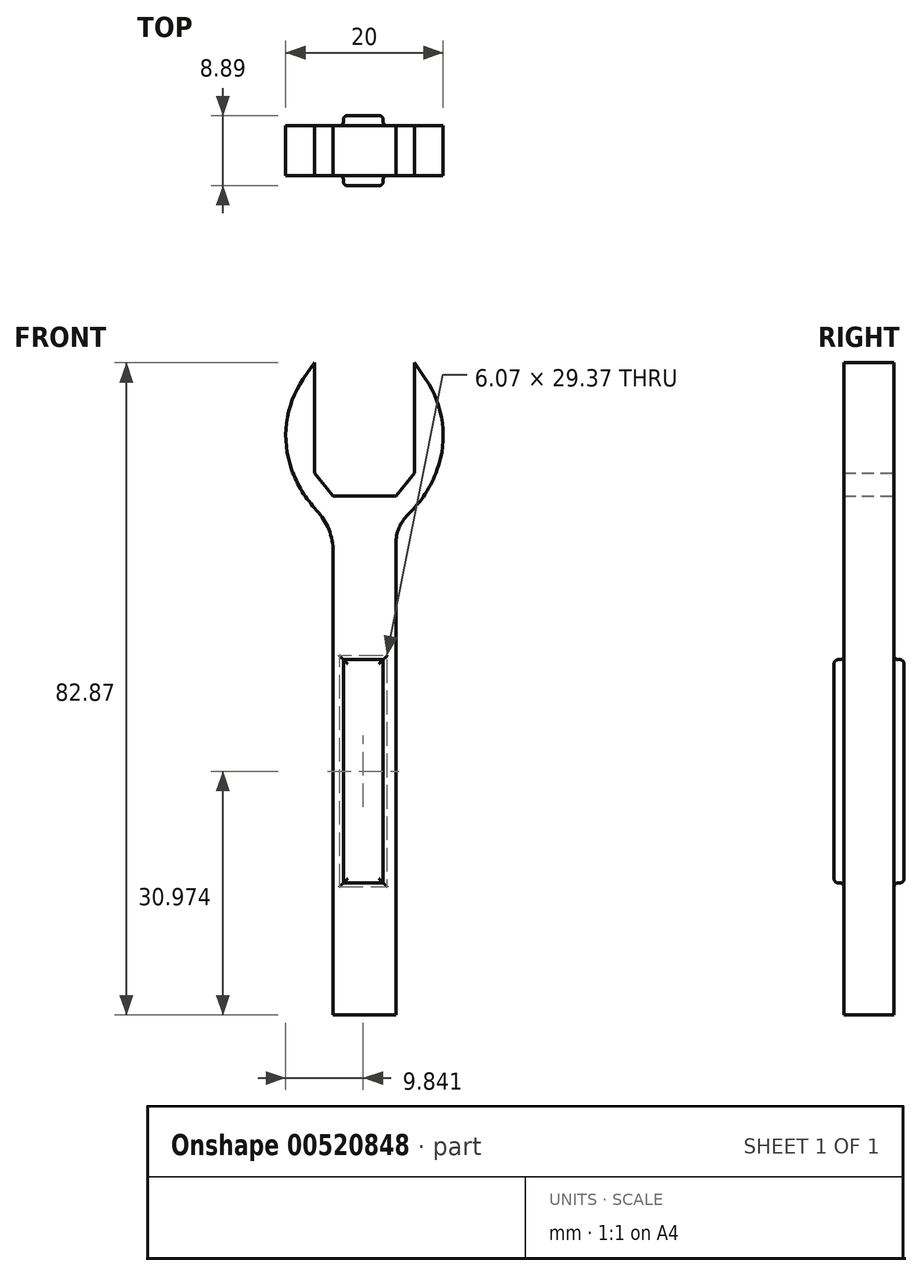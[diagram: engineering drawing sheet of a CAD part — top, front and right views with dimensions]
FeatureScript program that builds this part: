
annotation { "Feature Type Name" : "Feature", "Feature Type Description" : "" }
export const myFeature = defineFeature(function(context is Context, id is Id, definition is map)
    precondition{}
    {
        {
            var Q0;
            Q0=qCreatedBy(makeId("Front.planeOp"),FACE);
            var sketch = newSketch(context, id + "F0", { "sketchPlane" : qUnion([Q0])});
            skLineSegment(sketch, "E0", {"start": v(-17.48, 44.08) * mm, "end": v(-17.48, -18.2) * mm});
            skLineSegment(sketch, "E1", {"start": v(-9.5, -18.2) * mm, "end": v(-9.5, 44.08) * mm});
            skLineSegment(sketch, "E2", {"start": v(-17.48, 44.08) * mm, "end": v(-9.5, 44.08) * mm});
            skLineSegment(sketch, "E3", {"start": v(-9.5, 47.76) * mm, "end": v(-17.48, 47.76) * mm});
            skLineSegment(sketch, "E4", {"start": v(-17.48, 47.76) * mm, "end": v(-19.84, 50.66) * mm});
            skLineSegment(sketch, "E5", {"start": v(-19.84, 50.66) * mm, "end": v(-19.84, 59.78) * mm});
            skLineSegment(sketch, "E6", {"start": v(-19.84, 59.78) * mm, "end": v(-23.2, 59.78) * mm});
            skArc(sketch, "E7", {"start": v(-23.2, 59.78) * mm, "mid": v(-22.72, 51.06) * mm, "end": v(-17.48, 44.08) * mm});
            skLineSegment(sketch, "E8.MirrorCS", {"start": v(-7.14, 50.66) * mm, "end": v(-7.14, 59.78) * mm});
            skLineSegment(sketch, "E9.MirrorCS", {"start": v(-7.14, 59.78) * mm, "end": v(-3.79, 59.78) * mm});
            skLineSegment(sketch, "E10.MirrorCS", {"start": v(-17.48, 47.76) * mm, "end": v(-9.5, 47.76) * mm});
            skLineSegment(sketch, "E11.MirrorCS", {"start": v(-9.5, 47.76) * mm, "end": v(-7.14, 50.66) * mm});
            skArc(sketch, "E12.MirrorCS", {"start": v(-3.79, 59.78) * mm, "mid": v(-4.26, 51.06) * mm, "end": v(-9.5, 44.08) * mm});
            skLineSegment(sketch, "E13.MirrorCS", {"start": v(-9.5, 44.08) * mm, "end": v(-17.48, 44.08) * mm});
            skLineSegment(sketch, "E14", {"start": v(-23.2, 59.78) * mm, "end": v(-19.84, 64.68) * mm});
            skLineSegment(sketch, "E15", {"start": v(-19.84, 64.68) * mm, "end": v(-19.84, 59.78) * mm});
            skLineSegment(sketch, "E16", {"start": v(-7.14, 59.78) * mm, "end": v(-7.14, 64.68) * mm});
            skLineSegment(sketch, "E17", {"start": v(-7.14, 64.68) * mm, "end": v(-3.79, 59.78) * mm});
            skPoint(sketch, "E18.endSnap0", {"position": v(-17.48, 12.95) * mm});
            skLineSegment(sketch, "E19", {"start": v(-17.48, -18.2) * mm, "end": v(-9.5, -18.2) * mm});
            skSolve(sketch);
        }
        {
            var Q0;
            Q0 = qSketchRegion(id + "F0", true);
            extrude(context, id + "F1", {"entities" : qUnion([Q0]), "depth" : 6.35 * mm, "offsetDistance" : 25.4 * mm});
        }
        {
            var Q0;
            Q0=makeQuery(id+"F1.opExtrude","SWEPT_EDGE",EDGE,{"disambiguationData":[OSD([sQuery(id+"F0.wireOp",EDGE,"E0"),sQuery(id+"F0.wireOp",EDGE,"E7"),sQuery(id+"F0.wireOp",EDGE,"E13.MirrorCS")])]});
            fillet(context, id + "F2", {"entities" : qUnion([Q0]), "radius" : 7.62 * mm, "tangentPropagation" : true, "allowEdgeOverflow" : false});
        }
        {
            var Q0;
            Q0=makeQuery(id+"F1.opExtrude","SWEPT_EDGE",EDGE,{"disambiguationData":[OSD([sQuery(id+"F0.wireOp",EDGE,"E12.MirrorCS"),sQuery(id+"F0.wireOp",EDGE,"E9.MirrorCS"),sQuery(id+"F0.wireOp",EDGE,"E17")])]});
            var Q1;
            Q1=makeQuery(id+"F1.opExtrude","SWEPT_EDGE",EDGE,{"disambiguationData":[OSD([sQuery(id+"F0.wireOp",EDGE,"E6"),sQuery(id+"F0.wireOp",EDGE,"E7"),sQuery(id+"F0.wireOp",EDGE,"E14")])]});
            fillet(context, id + "F3", {"entities" : qUnion([Q0, Q1]), "radius" : 12.7 * mm, "tangentPropagation" : true, "allowEdgeOverflow" : false});
        }
        {
            var Q0;
            Q0=makeQuery(id+"F1.opExtrude","CAP_FACE",FACE,{"disambiguationData":[OSD([sQuery(id+"F0.wireOp",EDGE,"E0"),sQuery(id+"F0.wireOp",EDGE,"E1"),sQuery(id+"F0.wireOp",EDGE,"E7"),sQuery(id+"F0.wireOp",EDGE,"E4"),sQuery(id+"F0.wireOp",EDGE,"E8.MirrorCS"),sQuery(id+"F0.wireOp",EDGE,"E12.MirrorCS"),sQuery(id+"F0.wireOp",EDGE,"E3"),sQuery(id+"F0.wireOp",EDGE,"E11.MirrorCS"),sQuery(id+"F0.wireOp",EDGE,"E5"),sQuery(id+"F0.wireOp",EDGE,"E14"),sQuery(id+"F0.wireOp",EDGE,"E15"),sQuery(id+"F0.wireOp",EDGE,"E16"),sQuery(id+"F0.wireOp",EDGE,"E17"),sQuery(id+"F0.wireOp",EDGE,"E19")])],"isStart":true});
            var sketch = newSketch(context, id + "F4", { "sketchPlane" : qUnion([Q0])});
            skLineSegment(sketch, "E20.bottom", {"start": v(11.12, -1.4) * mm, "end": v(16.17, -1.4) * mm});
            skLineSegment(sketch, "E20.top", {"start": v(11.12, 26.96) * mm, "end": v(16.17, 26.96) * mm});
            skLineSegment(sketch, "E20.left", {"start": v(11.12, -1.4) * mm, "end": v(11.12, 26.96) * mm});
            skLineSegment(sketch, "E20.right", {"start": v(16.17, -1.4) * mm, "end": v(16.17, 26.96) * mm});
            skSolve(sketch);
        }
        {
            var Q0;
            Q0=makeQuery(id+"F4.imprint","IMPRINT",FACE,{"disambiguationData":[TD([[makeQuery(id+"F4.imprint","IMPRINT",EDGE,{"derivedFrom":sQuery(id+"F4.wireOp",EDGE,"E20.bottom")}),1.0]])]});
            extrude(context, id + "F5", {"entities" : qUnion([Q0]), "operationType" : NewBodyOperationType.ADD, "oppositeDirection" : true, "depth" : 7.62 * mm, "offsetDistance" : 25.4 * mm, "hasSecondDirection" : true, "secondDirectionOppositeDirection" : false, "secondDirectionDepth" : 1.27 * mm});
        }
        {
            var Q0;
            Q0=makeQuery(id+"F5.boolean.opBoolean","INTERSECT",EDGE,{"derivedFrom":[makeQuery(id+"F1.opExtrude","CAP_FACE",FACE,{"disambiguationData":[OSD([sQuery(id+"F0.wireOp",EDGE,"E0"),sQuery(id+"F0.wireOp",EDGE,"E1"),sQuery(id+"F0.wireOp",EDGE,"E7"),sQuery(id+"F0.wireOp",EDGE,"E4"),sQuery(id+"F0.wireOp",EDGE,"E8.MirrorCS"),sQuery(id+"F0.wireOp",EDGE,"E12.MirrorCS"),sQuery(id+"F0.wireOp",EDGE,"E3"),sQuery(id+"F0.wireOp",EDGE,"E11.MirrorCS"),sQuery(id+"F0.wireOp",EDGE,"E5"),sQuery(id+"F0.wireOp",EDGE,"E14"),sQuery(id+"F0.wireOp",EDGE,"E15"),sQuery(id+"F0.wireOp",EDGE,"E16"),sQuery(id+"F0.wireOp",EDGE,"E17"),sQuery(id+"F0.wireOp",EDGE,"E19")])],"isStart":true}),makeQuery(id+"F5.opExtrude","SWEPT_FACE",FACE,{"disambiguationData":[OSD([sQuery(id+"F4.wireOp",EDGE,"E20.left")])]})]});
            var Q1;
            Q1=makeQuery(id+"F5.boolean.opBoolean","INTERSECT",EDGE,{"derivedFrom":[makeQuery(id+"F1.opExtrude","CAP_FACE",FACE,{"disambiguationData":[OSD([sQuery(id+"F0.wireOp",EDGE,"E0"),sQuery(id+"F0.wireOp",EDGE,"E1"),sQuery(id+"F0.wireOp",EDGE,"E7"),sQuery(id+"F0.wireOp",EDGE,"E4"),sQuery(id+"F0.wireOp",EDGE,"E8.MirrorCS"),sQuery(id+"F0.wireOp",EDGE,"E12.MirrorCS"),sQuery(id+"F0.wireOp",EDGE,"E3"),sQuery(id+"F0.wireOp",EDGE,"E11.MirrorCS"),sQuery(id+"F0.wireOp",EDGE,"E5"),sQuery(id+"F0.wireOp",EDGE,"E14"),sQuery(id+"F0.wireOp",EDGE,"E15"),sQuery(id+"F0.wireOp",EDGE,"E16"),sQuery(id+"F0.wireOp",EDGE,"E17"),sQuery(id+"F0.wireOp",EDGE,"E19")])],"isStart":true}),makeQuery(id+"F5.opExtrude","SWEPT_FACE",FACE,{"disambiguationData":[OSD([sQuery(id+"F4.wireOp",EDGE,"E20.bottom")])]})]});
            var Q2;
            Q2=makeQuery(id+"F5.boolean.opBoolean","INTERSECT",EDGE,{"derivedFrom":[makeQuery(id+"F1.opExtrude","CAP_FACE",FACE,{"disambiguationData":[OSD([sQuery(id+"F0.wireOp",EDGE,"E0"),sQuery(id+"F0.wireOp",EDGE,"E1"),sQuery(id+"F0.wireOp",EDGE,"E7"),sQuery(id+"F0.wireOp",EDGE,"E4"),sQuery(id+"F0.wireOp",EDGE,"E8.MirrorCS"),sQuery(id+"F0.wireOp",EDGE,"E12.MirrorCS"),sQuery(id+"F0.wireOp",EDGE,"E3"),sQuery(id+"F0.wireOp",EDGE,"E11.MirrorCS"),sQuery(id+"F0.wireOp",EDGE,"E5"),sQuery(id+"F0.wireOp",EDGE,"E14"),sQuery(id+"F0.wireOp",EDGE,"E15"),sQuery(id+"F0.wireOp",EDGE,"E16"),sQuery(id+"F0.wireOp",EDGE,"E17"),sQuery(id+"F0.wireOp",EDGE,"E19")])],"isStart":true}),makeQuery(id+"F5.opExtrude","SWEPT_FACE",FACE,{"disambiguationData":[OSD([sQuery(id+"F4.wireOp",EDGE,"E20.top")])]})]});
            var Q3;
            Q3=makeQuery(id+"F5.boolean.opBoolean","INTERSECT",EDGE,{"derivedFrom":[makeQuery(id+"F1.opExtrude","CAP_FACE",FACE,{"disambiguationData":[OSD([sQuery(id+"F0.wireOp",EDGE,"E0"),sQuery(id+"F0.wireOp",EDGE,"E1"),sQuery(id+"F0.wireOp",EDGE,"E7"),sQuery(id+"F0.wireOp",EDGE,"E4"),sQuery(id+"F0.wireOp",EDGE,"E8.MirrorCS"),sQuery(id+"F0.wireOp",EDGE,"E12.MirrorCS"),sQuery(id+"F0.wireOp",EDGE,"E3"),sQuery(id+"F0.wireOp",EDGE,"E11.MirrorCS"),sQuery(id+"F0.wireOp",EDGE,"E5"),sQuery(id+"F0.wireOp",EDGE,"E14"),sQuery(id+"F0.wireOp",EDGE,"E15"),sQuery(id+"F0.wireOp",EDGE,"E16"),sQuery(id+"F0.wireOp",EDGE,"E17"),sQuery(id+"F0.wireOp",EDGE,"E19")])],"isStart":true}),makeQuery(id+"F5.opExtrude","SWEPT_FACE",FACE,{"disambiguationData":[OSD([sQuery(id+"F4.wireOp",EDGE,"E20.right")])]})]});
            fillet(context, id + "F6", {"entities" : qUnion([Q0, Q1, Q2, Q3]), "radius" : 0.5 * mm, "tangentPropagation" : true, "allowEdgeOverflow" : false});
        }
        {
            var Q0;
            Q0=makeQuery(id+"F5.opExtrude","CAP_FACE",FACE,{"disambiguationData":[OSD([sQuery(id+"F4.wireOp",EDGE,"E20.bottom"),sQuery(id+"F4.wireOp",EDGE,"E20.top"),sQuery(id+"F4.wireOp",EDGE,"E20.left"),sQuery(id+"F4.wireOp",EDGE,"E20.right")])],"isStart":true});
            fillet(context, id + "F7", {"entities" : qUnion([Q0]), "radius" : 0.5 * mm, "tangentPropagation" : true, "allowEdgeOverflow" : false});
        }
        {
            var Q0;
            Q0=makeQuery(id+"F5.boolean.opBoolean","INTERSECT",EDGE,{"derivedFrom":[makeQuery(id+"F1.opExtrude","CAP_FACE",FACE,{"disambiguationData":[OSD([sQuery(id+"F0.wireOp",EDGE,"E0"),sQuery(id+"F0.wireOp",EDGE,"E1"),sQuery(id+"F0.wireOp",EDGE,"E7"),sQuery(id+"F0.wireOp",EDGE,"E4"),sQuery(id+"F0.wireOp",EDGE,"E8.MirrorCS"),sQuery(id+"F0.wireOp",EDGE,"E12.MirrorCS"),sQuery(id+"F0.wireOp",EDGE,"E3"),sQuery(id+"F0.wireOp",EDGE,"E11.MirrorCS"),sQuery(id+"F0.wireOp",EDGE,"E5"),sQuery(id+"F0.wireOp",EDGE,"E14"),sQuery(id+"F0.wireOp",EDGE,"E15"),sQuery(id+"F0.wireOp",EDGE,"E16"),sQuery(id+"F0.wireOp",EDGE,"E17"),sQuery(id+"F0.wireOp",EDGE,"E19")])],"isStart":false}),makeQuery(id+"F5.opExtrude","SWEPT_FACE",FACE,{"disambiguationData":[OSD([sQuery(id+"F4.wireOp",EDGE,"E20.bottom")])]})]});
            var Q1;
            Q1=makeQuery(id+"F5.boolean.opBoolean","INTERSECT",EDGE,{"derivedFrom":[makeQuery(id+"F1.opExtrude","CAP_FACE",FACE,{"disambiguationData":[OSD([sQuery(id+"F0.wireOp",EDGE,"E0"),sQuery(id+"F0.wireOp",EDGE,"E1"),sQuery(id+"F0.wireOp",EDGE,"E7"),sQuery(id+"F0.wireOp",EDGE,"E4"),sQuery(id+"F0.wireOp",EDGE,"E8.MirrorCS"),sQuery(id+"F0.wireOp",EDGE,"E12.MirrorCS"),sQuery(id+"F0.wireOp",EDGE,"E3"),sQuery(id+"F0.wireOp",EDGE,"E11.MirrorCS"),sQuery(id+"F0.wireOp",EDGE,"E5"),sQuery(id+"F0.wireOp",EDGE,"E14"),sQuery(id+"F0.wireOp",EDGE,"E15"),sQuery(id+"F0.wireOp",EDGE,"E16"),sQuery(id+"F0.wireOp",EDGE,"E17"),sQuery(id+"F0.wireOp",EDGE,"E19")])],"isStart":false}),makeQuery(id+"F5.opExtrude","SWEPT_FACE",FACE,{"disambiguationData":[OSD([sQuery(id+"F4.wireOp",EDGE,"E20.left")])]})]});
            var Q2;
            Q2=makeQuery(id+"F5.boolean.opBoolean","INTERSECT",EDGE,{"derivedFrom":[makeQuery(id+"F1.opExtrude","CAP_FACE",FACE,{"disambiguationData":[OSD([sQuery(id+"F0.wireOp",EDGE,"E0"),sQuery(id+"F0.wireOp",EDGE,"E1"),sQuery(id+"F0.wireOp",EDGE,"E7"),sQuery(id+"F0.wireOp",EDGE,"E4"),sQuery(id+"F0.wireOp",EDGE,"E8.MirrorCS"),sQuery(id+"F0.wireOp",EDGE,"E12.MirrorCS"),sQuery(id+"F0.wireOp",EDGE,"E3"),sQuery(id+"F0.wireOp",EDGE,"E11.MirrorCS"),sQuery(id+"F0.wireOp",EDGE,"E5"),sQuery(id+"F0.wireOp",EDGE,"E14"),sQuery(id+"F0.wireOp",EDGE,"E15"),sQuery(id+"F0.wireOp",EDGE,"E16"),sQuery(id+"F0.wireOp",EDGE,"E17"),sQuery(id+"F0.wireOp",EDGE,"E19")])],"isStart":false}),makeQuery(id+"F5.opExtrude","SWEPT_FACE",FACE,{"disambiguationData":[OSD([sQuery(id+"F4.wireOp",EDGE,"E20.top")])]})]});
            var Q3;
            Q3=makeQuery(id+"F5.boolean.opBoolean","INTERSECT",EDGE,{"derivedFrom":[makeQuery(id+"F1.opExtrude","CAP_FACE",FACE,{"disambiguationData":[OSD([sQuery(id+"F0.wireOp",EDGE,"E0"),sQuery(id+"F0.wireOp",EDGE,"E1"),sQuery(id+"F0.wireOp",EDGE,"E7"),sQuery(id+"F0.wireOp",EDGE,"E4"),sQuery(id+"F0.wireOp",EDGE,"E8.MirrorCS"),sQuery(id+"F0.wireOp",EDGE,"E12.MirrorCS"),sQuery(id+"F0.wireOp",EDGE,"E3"),sQuery(id+"F0.wireOp",EDGE,"E11.MirrorCS"),sQuery(id+"F0.wireOp",EDGE,"E5"),sQuery(id+"F0.wireOp",EDGE,"E14"),sQuery(id+"F0.wireOp",EDGE,"E15"),sQuery(id+"F0.wireOp",EDGE,"E16"),sQuery(id+"F0.wireOp",EDGE,"E17"),sQuery(id+"F0.wireOp",EDGE,"E19")])],"isStart":false}),makeQuery(id+"F5.opExtrude","SWEPT_FACE",FACE,{"disambiguationData":[OSD([sQuery(id+"F4.wireOp",EDGE,"E20.right")])]})]});
            var Q4;
            Q4=makeQuery(id+"F5.opExtrude","CAP_FACE",FACE,{"disambiguationData":[OSD([sQuery(id+"F4.wireOp",EDGE,"E20.bottom"),sQuery(id+"F4.wireOp",EDGE,"E20.top"),sQuery(id+"F4.wireOp",EDGE,"E20.left"),sQuery(id+"F4.wireOp",EDGE,"E20.right")])],"isStart":false});
            fillet(context, id + "F8", {"entities" : qUnion([Q0, Q1, Q2, Q3, Q4]), "radius" : 0.5 * mm, "tangentPropagation" : true, "allowEdgeOverflow" : false});
        }
        {
            var Q0;
            Q0=makeQuery(id+"F1.opExtrude","SWEPT_EDGE",EDGE,{"disambiguationData":[OSD([sQuery(id+"F0.wireOp",EDGE,"E1"),sQuery(id+"F0.wireOp",EDGE,"E12.MirrorCS"),sQuery(id+"F0.wireOp",EDGE,"E13.MirrorCS")])]});
            fillet(context, id + "F9", {"entities" : qUnion([Q0]), "radius" : 5.08 * mm, "tangentPropagation" : true, "allowEdgeOverflow" : false});
        }
    });
